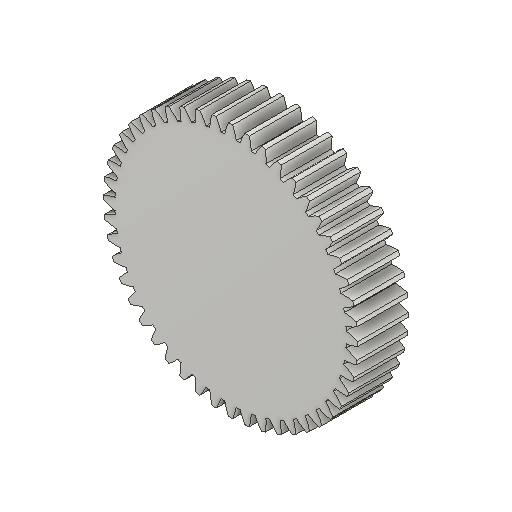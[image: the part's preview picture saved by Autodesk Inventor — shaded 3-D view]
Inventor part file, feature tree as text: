
AUTODESK INVENTOR PART (.ipt)
format: ipt  version: 2024 (Build 280153000, 153)  size: 332,800 bytes
history: native  units: mm (DEFAULTED — no unit token found)
features: plane x3, other x3, extrude x1, sketch x1
ambient origin geometry x8: Origin, YZ Plane, XZ Plane, XY Plane, X Axis, Y Axis, Z Axis, Center Point
bodies: Solid1 (feature_tree)
feature tree (8):
  extrude  "Extrusion1"  Depth=20.0mm TaperAngle=0.0deg
  plane  "Work Plane2"
  plane  "Work Plane8"
  plane  "Work Plane9"
  other  "Spur Gear"
  sketch  "Sketch1"  dims[d0=100.0mm d1=20.0mm d2=0.0mm d3=96.0mm d4=10.0mm d5=0.0mm d16=60.0mm d17=0.0mm d34=0.654498mm d39=0.0mm d41=0.0mm d43=60.0mm d46=60.0mm d47=0.0mm d48=0.0mm]
  other  "Srf1"
  other  "Pitch Diameter"
